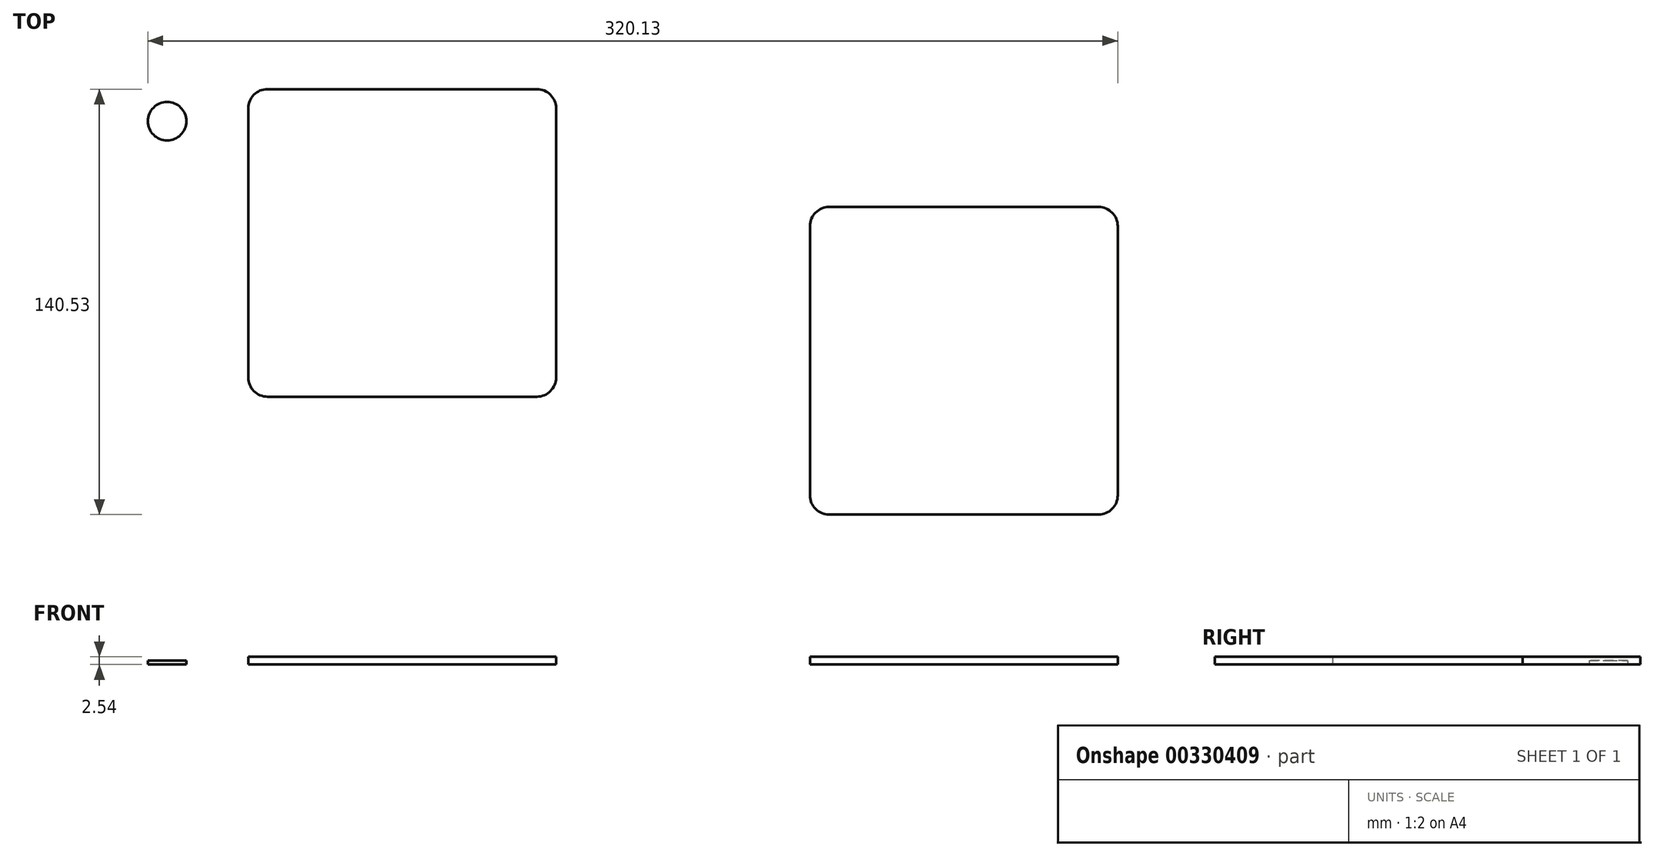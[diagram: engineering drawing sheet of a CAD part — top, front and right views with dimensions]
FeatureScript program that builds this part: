
annotation { "Feature Type Name" : "Feature", "Feature Type Description" : "" }
export const myFeature = defineFeature(function(context is Context, id is Id, definition is map)
    precondition{}
    {
        {
            var Q0;
            Q0=qCreatedBy(makeId("Top.planeOp"),FACE);
            var sketch = newSketch(context, id + "F0", { "sketchPlane" : qUnion([Q0])});
            skLineSegment(sketch, "E0.bottom", {"start": v(-39.37, -38.48) * mm, "end": v(49.53, -38.48) * mm});
            skLineSegment(sketch, "E0.top", {"start": v(-39.37, 63.12) * mm, "end": v(49.53, 63.12) * mm});
            skLineSegment(sketch, "E0.left", {"start": v(-45.72, -32.13) * mm, "end": v(-45.72, 56.77) * mm});
            skLineSegment(sketch, "E0.right", {"start": v(55.88, -32.13) * mm, "end": v(55.88, 56.77) * mm});
            skPoint(sketch, "E1.visualSharp", {"position": v(-45.72, 63.12) * mm});
            skArc(sketch, "E1.filletArc", {"start": v(-39.37, 63.12) * mm, "mid": v(-43.86, 61.26) * mm, "end": v(-45.72, 56.77) * mm});
            skPoint(sketch, "E2.visualSharp", {"position": v(55.88, 63.12) * mm});
            skArc(sketch, "E2.filletArc", {"start": v(55.88, 56.77) * mm, "mid": v(54.02, 61.26) * mm, "end": v(49.53, 63.12) * mm});
            skPoint(sketch, "E3.visualSharp", {"position": v(55.88, -38.48) * mm});
            skArc(sketch, "E3.filletArc", {"start": v(49.53, -38.48) * mm, "mid": v(54.02, -36.62) * mm, "end": v(55.88, -32.13) * mm});
            skPoint(sketch, "E4.visualSharp", {"position": v(-45.72, -38.48) * mm});
            skArc(sketch, "E4.filletArc", {"start": v(-45.72, -32.13) * mm, "mid": v(-43.86, -36.62) * mm, "end": v(-39.37, -38.48) * mm});
            skSolve(sketch);
        }
        {
            var Q0;
            Q0=makeQuery(id+"F0.imprint","IMPRINT",FACE,{"disambiguationData":[TD([[makeQuery(id+"F0.imprint","IMPRINT",EDGE,{"derivedFrom":sQuery(id+"F0.wireOp",EDGE,"E0.bottom")}),1.0]])]});
            extrude(context, id + "F1", {"entities" : qUnion([Q0]), "depth" : 2.54 * mm});
        }
        {
            var Q0;
            Q0=qCreatedBy(makeId("Top.planeOp"),FACE);
            var sketch = newSketch(context, id + "F2", { "sketchPlane" : qUnion([Q0])});
            skCircle(sketch, "E5", {"center": v(-72.5, 52.53) * mm, "radius": 6.35 * mm});
            skSolve(sketch);
        }
        {
            var Q0;
            Q0 = qSketchRegion(id + "F2", true);
            extrude(context, id + "F3", {"entities" : qUnion([Q0]), "depth" : 1.27 * mm});
        }
        {
            var Q0;
            Q0=qCreatedBy(makeId("Top.planeOp"),FACE);
            var sketch = newSketch(context, id + "F4", { "sketchPlane" : qUnion([Q0])});
            skLineSegment(sketch, "E6.bottom", {"start": v(146.02, 24.19) * mm, "end": v(234.92, 24.19) * mm});
            skLineSegment(sketch, "E6.top", {"start": v(146.02, -77.41) * mm, "end": v(234.92, -77.41) * mm});
            skLineSegment(sketch, "E6.left", {"start": v(139.67, 17.84) * mm, "end": v(139.67, -71.06) * mm});
            skLineSegment(sketch, "E6.right", {"start": v(241.27, 17.84) * mm, "end": v(241.27, -71.06) * mm});
            skPoint(sketch, "E7.visualSharp", {"position": v(139.67, 24.19) * mm});
            skArc(sketch, "E7.filletArc", {"start": v(146.02, 24.19) * mm, "mid": v(141.53, 22.33) * mm, "end": v(139.67, 17.84) * mm});
            skPoint(sketch, "E8.visualSharp", {"position": v(139.67, -77.41) * mm});
            skArc(sketch, "E8.filletArc", {"start": v(139.67, -71.06) * mm, "mid": v(141.53, -75.55) * mm, "end": v(146.02, -77.41) * mm});
            skPoint(sketch, "E9.visualSharp", {"position": v(241.27, -77.41) * mm});
            skArc(sketch, "E9.filletArc", {"start": v(234.92, -77.41) * mm, "mid": v(239.4, -75.55) * mm, "end": v(241.27, -71.06) * mm});
            skPoint(sketch, "E10.visualSharp", {"position": v(241.27, 24.19) * mm});
            skArc(sketch, "E10.filletArc", {"start": v(241.27, 17.84) * mm, "mid": v(239.4, 22.33) * mm, "end": v(234.92, 24.19) * mm});
            skSolve(sketch);
        }
        {
            var Q0;
            Q0 = qSketchRegion(id + "F4", true);
            extrude(context, id + "F5", {"entities" : qUnion([Q0]), "depth" : 2.54 * mm});
        }
    });
